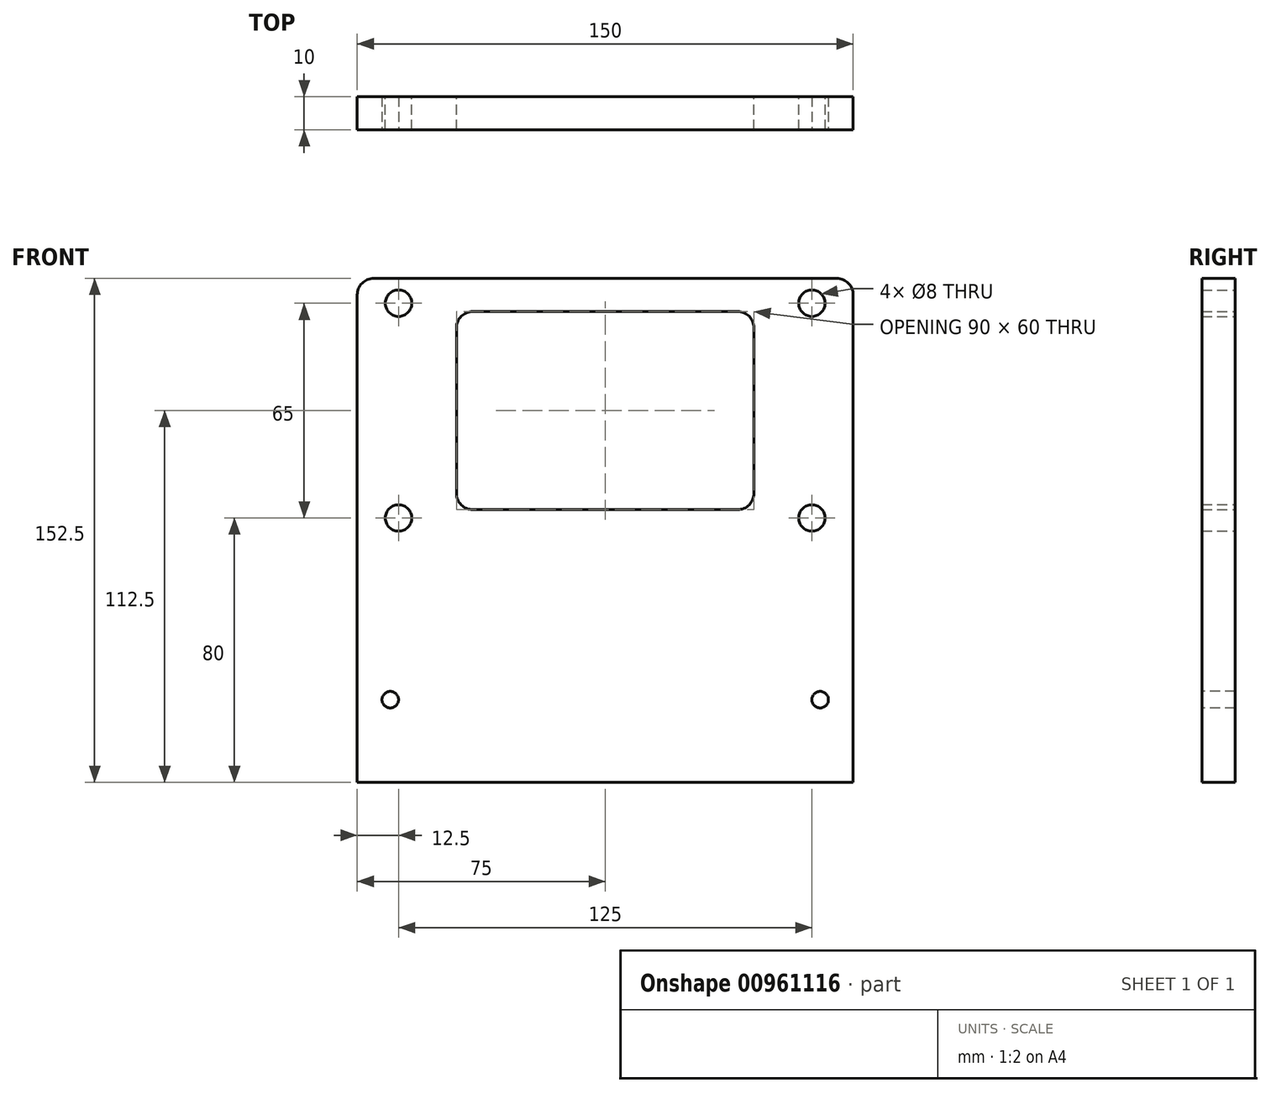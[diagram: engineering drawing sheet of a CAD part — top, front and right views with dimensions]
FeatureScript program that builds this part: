
annotation { "Feature Type Name" : "Feature", "Feature Type Description" : "" }
export const myFeature = defineFeature(function(context is Context, id is Id, definition is map)
    precondition{}
    {
        {
            var Q0;
            Q0=qCreatedBy(makeId("Front.planeOp"),FACE);
            var sketch = newSketch(context, id + "F0", { "sketchPlane" : qUnion([Q0])});
            skLineSegment(sketch, "E0.bottom", {"start": v(40, 30) * mm, "end": v(-40, 30) * mm});
            skLineSegment(sketch, "E0.top", {"start": v(40, -30) * mm, "end": v(-40, -30) * mm});
            skLineSegment(sketch, "E0.left", {"start": v(45, 25) * mm, "end": v(45, -25) * mm});
            skLineSegment(sketch, "E0.right", {"start": v(-45, 25) * mm, "end": v(-45, -25) * mm});
            skPoint(sketch, "E0.middle", {"position": v(0, 0) * mm});
            skLineSegment(sketch, "E1", {"start": v(-75, 40) * mm, "end": v(75, 40) * mm});
            skLineSegment(sketch, "E2", {"start": v(75, 40) * mm, "end": v(75, -112.5) * mm});
            skLineSegment(sketch, "E3", {"start": v(-75, 40) * mm, "end": v(-75, -112.5) * mm});
            skLineSegment(sketch, "E4", {"start": v(75, -112.5) * mm, "end": v(-75, -112.5) * mm});
            skCircle(sketch, "E5", {"center": v(-62.5, 32.5) * mm, "radius": 4 * mm});
            skLineSegment(sketch, "E6", {"start": v(0, 40) * mm, "end": v(0, -112.5) * mm, "construction": true});
            skLineSegment(sketch, "E7", {"start": v(75, 0) * mm, "end": v(-75, 0) * mm, "construction": true});
            skCircle(sketch, "E8.MirrorC", {"center": v(-62.5, -32.5) * mm, "radius": 4 * mm});
            skCircle(sketch, "E9.MirrorC", {"center": v(62.5, 32.5) * mm, "radius": 4 * mm});
            skCircle(sketch, "E10.MirrorC", {"center": v(62.5, -32.5) * mm, "radius": 4 * mm});
            skPoint(sketch, "E11.visualSharp", {"position": v(-45, 30) * mm});
            skArc(sketch, "E11.filletArc", {"start": v(-40, 30) * mm, "mid": v(-43.54, 28.54) * mm, "end": v(-45, 25) * mm});
            skPoint(sketch, "E12.visualSharp", {"position": v(45, 30) * mm});
            skArc(sketch, "E12.filletArc", {"start": v(45, 25) * mm, "mid": v(43.54, 28.54) * mm, "end": v(40, 30) * mm});
            skPoint(sketch, "E13.visualSharp", {"position": v(45, -30) * mm});
            skArc(sketch, "E13.filletArc", {"start": v(40, -30) * mm, "mid": v(43.54, -28.54) * mm, "end": v(45, -25) * mm});
            skPoint(sketch, "E14.visualSharp", {"position": v(-45, -30) * mm});
            skArc(sketch, "E14.filletArc", {"start": v(-45, -25) * mm, "mid": v(-43.54, -28.54) * mm, "end": v(-40, -30) * mm});
            skSolve(sketch);
        }
        {
            var Q0;
            Q0 = qSketchRegion(id + "F0", true);
            extrude(context, id + "F1", {"entities" : qUnion([Q0]), "depth" : 10 * mm, "offsetDistance" : 25 * mm});
        }
        {
            var Q0;
            Q0=makeQuery(id+"F1.opExtrude","SWEPT_EDGE",EDGE,{"disambiguationData":[OSD([sQuery(id+"F0.wireOp",EDGE,"E1"),sQuery(id+"F0.wireOp",EDGE,"E3")])]});
            var Q1;
            Q1=makeQuery(id+"F1.opExtrude","SWEPT_EDGE",EDGE,{"disambiguationData":[OSD([sQuery(id+"F0.wireOp",EDGE,"E1"),sQuery(id+"F0.wireOp",EDGE,"E2")])]});
            fillet(context, id + "F2", {"entities" : qUnion([Q0, Q1]), "radius" : 5 * mm, "tangentPropagation" : true, "allowEdgeOverflow" : false});
        }
        {
            var Q0;
            Q0=makeQuery(id+"F1.opExtrude","CAP_FACE",FACE,{"disambiguationData":[OSD([sQuery(id+"F0.wireOp",EDGE,"E0.bottom"),sQuery(id+"F0.wireOp",EDGE,"E0.top"),sQuery(id+"F0.wireOp",EDGE,"E0.left"),sQuery(id+"F0.wireOp",EDGE,"E0.right"),sQuery(id+"F0.wireOp",EDGE,"E1"),sQuery(id+"F0.wireOp",EDGE,"E2"),sQuery(id+"F0.wireOp",EDGE,"E3"),sQuery(id+"F0.wireOp",EDGE,"E4"),sQuery(id+"F0.wireOp",EDGE,"E5"),sQuery(id+"F0.wireOp",EDGE,"E8.MirrorC"),sQuery(id+"F0.wireOp",EDGE,"E9.MirrorC"),sQuery(id+"F0.wireOp",EDGE,"E10.MirrorC"),sQuery(id+"F0.wireOp",EDGE,"E11.filletArc"),sQuery(id+"F0.wireOp",EDGE,"E12.filletArc"),sQuery(id+"F0.wireOp",EDGE,"E13.filletArc"),sQuery(id+"F0.wireOp",EDGE,"E14.filletArc")])],"isStart":false});
            var sketch = newSketch(context, id + "F3", { "sketchPlane" : qUnion([Q0])});
            skPoint(sketch, "E15", {"position": v(-65, -87.5) * mm});
            skPoint(sketch, "E16", {"position": v(65, -87.5) * mm});
            skSolve(sketch);
        }
        {
            var Q0;
            Q0=sQuery(id+"F3.wireOp",VERTEX,"E16");
            var Q1;
            Q1=sQuery(id+"F3.wireOp",VERTEX,"E15");
            var Q2;
            Q2=makeQuery(id+"F1.opExtrude","SWEPT_BODY",BODY,{"disambiguationData":[OSD([sQuery(id+"F0.wireOp",EDGE,"E0.bottom"),sQuery(id+"F0.wireOp",EDGE,"E0.top"),sQuery(id+"F0.wireOp",EDGE,"E0.left"),sQuery(id+"F0.wireOp",EDGE,"E0.right"),sQuery(id+"F0.wireOp",EDGE,"E1"),sQuery(id+"F0.wireOp",EDGE,"E2"),sQuery(id+"F0.wireOp",EDGE,"E3"),sQuery(id+"F0.wireOp",EDGE,"E4"),sQuery(id+"F0.wireOp",EDGE,"E5"),sQuery(id+"F0.wireOp",EDGE,"E8.MirrorC"),sQuery(id+"F0.wireOp",EDGE,"E9.MirrorC"),sQuery(id+"F0.wireOp",EDGE,"E10.MirrorC"),sQuery(id+"F0.wireOp",EDGE,"E11.filletArc"),sQuery(id+"F0.wireOp",EDGE,"E12.filletArc"),sQuery(id+"F0.wireOp",EDGE,"E13.filletArc"),sQuery(id+"F0.wireOp",EDGE,"E14.filletArc")])]});
            hole(context, id + "F4", {"style" : HoleStyle.SIMPLE, "endStyle" : HoleEndStyle.THROUGH, "standardTappedOrClearance" : lookupTablePath({ "standard" : "ISO", "engagement" : "75%", "pitch" : "1 mm", "size" : "M6", "type" : "Tapped" }), "standardBlindInLast" : lookupTablePath({ "standard" : "ISO", "fit" : "Normal", "engagement" : "75%", "pitch" : "1 mm", "size" : "M6", "type" : "Clearance & tapped" }), "holeDiameter" : 5 * mm, "majorDiameter" : 6 * mm, "showTappedDepth" : true, "tappedDepth" : 20 * mm, "tapClearance" : 3, "startFromSketch" : true, "locations" : qUnion([Q0, Q1]), "scope" : qUnion([Q2])});
        }
    });
